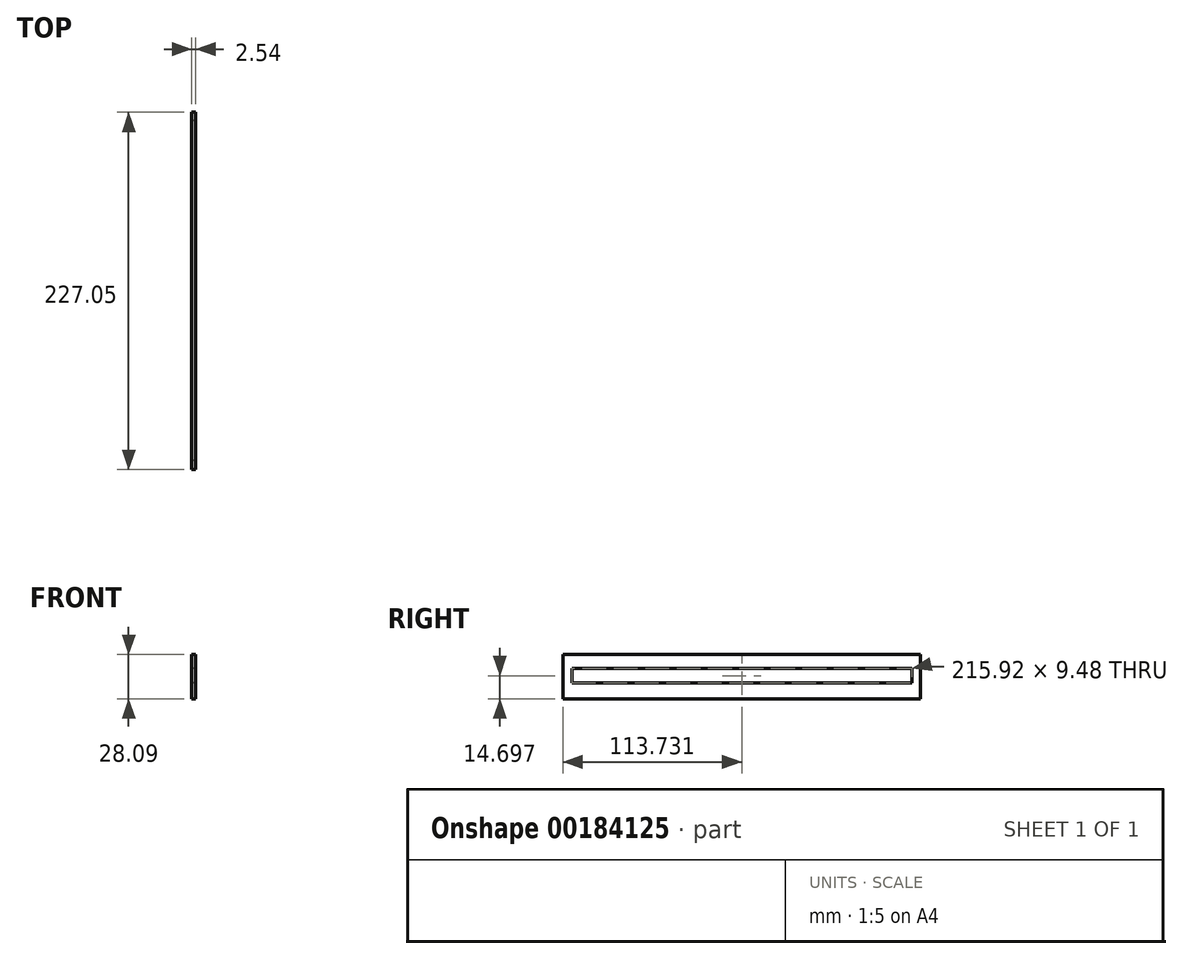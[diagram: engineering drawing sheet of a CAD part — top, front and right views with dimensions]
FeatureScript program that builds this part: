
annotation { "Feature Type Name" : "Feature", "Feature Type Description" : "" }
export const myFeature = defineFeature(function(context is Context, id is Id, definition is map)
    precondition{}
    {
        {
            var Q0;
            Q0=qCreatedBy(makeId("Right.planeOp"),FACE);
            var sketch = newSketch(context, id + "F0", { "sketchPlane" : qUnion([Q0])});
            skLineSegment(sketch, "E0", {"start": v(-99.72, 19.44) * mm, "end": v(-99.72, 9.96) * mm});
            skLineSegment(sketch, "E1", {"start": v(-99.72, 19.44) * mm, "end": v(116.2, 19.44) * mm});
            skLineSegment(sketch, "E2.top", {"start": v(-99.72, 9.96) * mm, "end": v(116.2, 9.96) * mm});
            skLineSegment(sketch, "E2.right", {"start": v(116.2, 19.44) * mm, "end": v(116.2, 9.96) * mm});
            skLineSegment(sketch, "E3.bottom", {"start": v(-105.49, 28.09) * mm, "end": v(121.56, 28.09) * mm});
            skLineSegment(sketch, "E3.top", {"start": v(-105.49, 0) * mm, "end": v(121.56, 0) * mm});
            skLineSegment(sketch, "E3.left", {"start": v(-105.49, 28.09) * mm, "end": v(-105.49, 0) * mm});
            skLineSegment(sketch, "E3.right", {"start": v(121.56, 28.09) * mm, "end": v(121.56, 0) * mm});
            skSolve(sketch);
        }
        {
            var Q0;
            Q0 = qSketchRegion(id + "F0", true);
            extrude(context, id + "F1", {"entities" : qUnion([Q0]), "depth" : 2.54 * mm});
        }
    });
